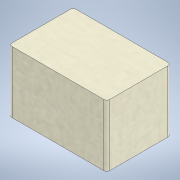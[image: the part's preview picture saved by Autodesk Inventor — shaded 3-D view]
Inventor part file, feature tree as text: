
AUTODESK INVENTOR PART (.ipt)
format: ipt  version: 2021 (Build 250183000, 183)  size: 118,784 bytes
history: native  units: mm
features: extrude x1, sketch x1
ambient origin geometry x8: Origin, YZ Plane, XZ Plane, XY Plane, X Axis, Y Axis, Z Axis, Center Point
bodies: Solid1 (feature_tree)
feature tree (2):
  extrude  "Extrusion1"  Depth=42.0mm
  sketch  "Sketch1"  dims[d0=64.0mm d1=42.0mm d2=2.0mm d3=40.4mm d4=0.0mm]
